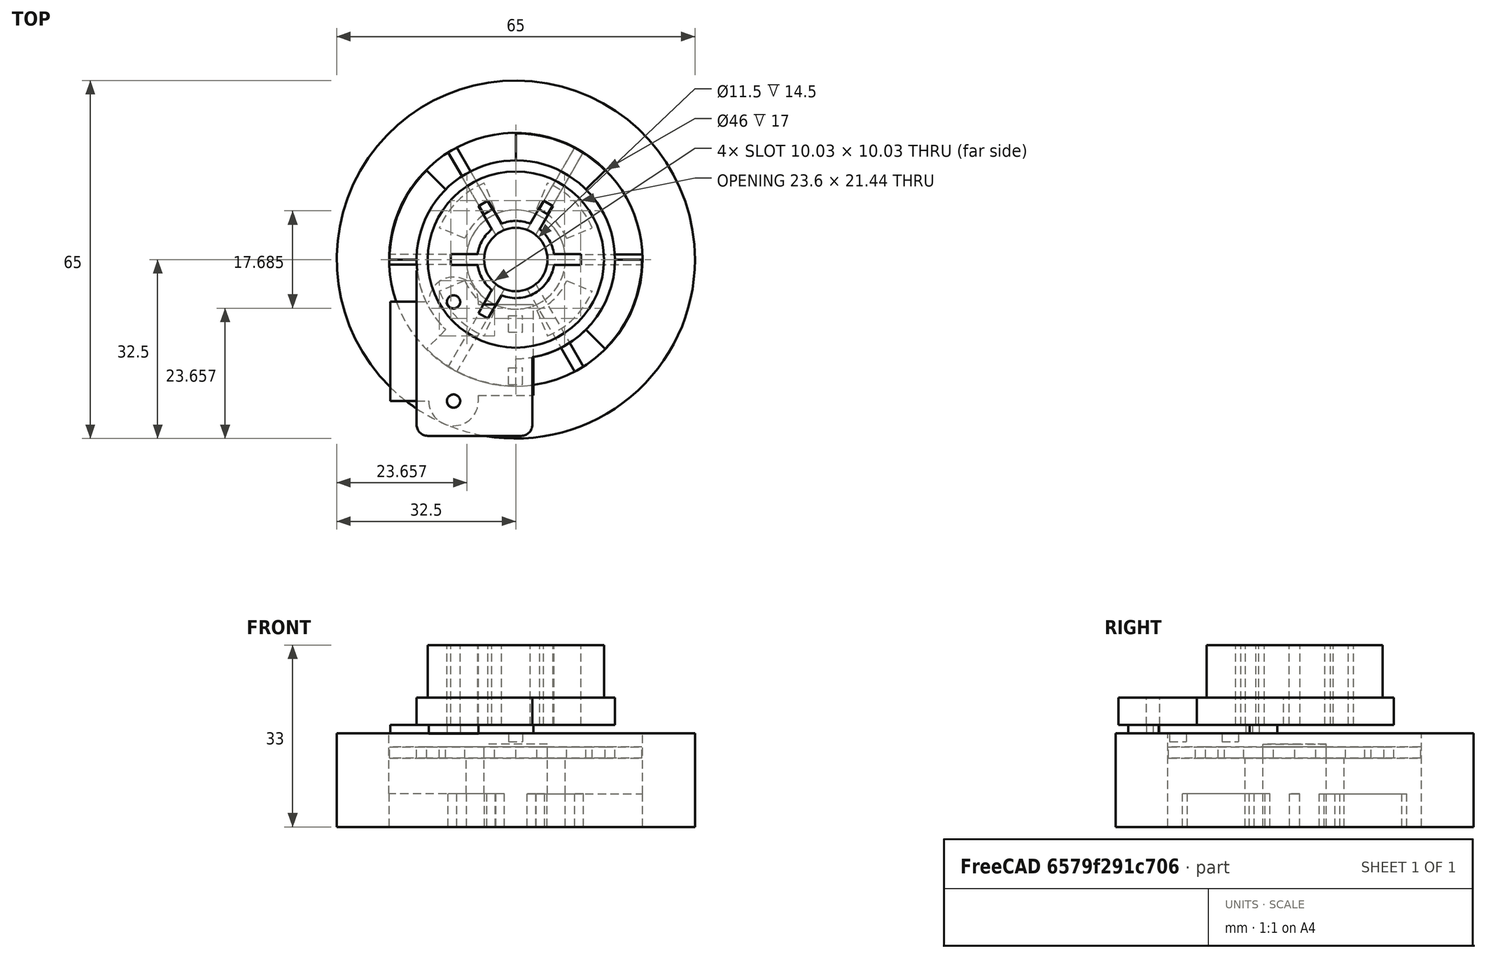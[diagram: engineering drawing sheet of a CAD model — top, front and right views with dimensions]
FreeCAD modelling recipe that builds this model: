
FCSTD DOCUMENT  (FreeCAD 0.15R4671 (Git))
Label: Encoder_wheel
License: All rights reserved
LicenseURL: http://es.wikipedia.org/wiki/Todos_los_derechos_reservados
objects: Part::Cylinder×14, Part::MultiFuse×10, Part::Cut×9, Part::Box×7, Part::FeaturePython×4, Part::Feature×2, Part::Extrusion×2, App::DocumentObjectGroup×1, Part::Fillet×1
note: 49 computed .brp shape members not serialized (recipe doc carries the construction recipe); baked Part::Feature solids carry a one-line shape summary decoded from their .brp

FEATURE [Part::Cylinder] Cylinder  label="Cilindro"
  Angle = 360
  Height = 15
  Radius = 5.75
FEATURE [Part::Box] Box  label="Cubo"
  Height = 6
  Length = 19
  Placement = pos=(5,-0.9,0) rot=(0,0,1;0rad)
  Width = 1.8
FEATURE [Part::FeaturePython] Array004  # Draft array (typed FeaturePython)
  Angle = 360
  ArrayType = 1
  Axis = (0,0,1)
  Base = -> Box
  Center = (0,0,0)
  Fuse = false
  IntervalAxis = (0,0,0)
  IntervalX = (1,0,0)
  IntervalY = (0,1,0)
  IntervalZ = (0,0,0)
  NumberPolar = 6
  NumberX = 2
  NumberY = 2
  NumberZ = 1
FEATURE [Part::MultiFuse] Fusion  label="Wheel_model"
  Shapes = -> [Cylinder,Array004]
FEATURE [Part::Cylinder] Cylinder002  label="Cilindro002"
  Angle = 360
  Height = 17
  Radius = 32.5
FEATURE [Part::Cylinder] Cylinder003  label="Cilindro003"
  Angle = 360
  Height = 17
  Radius = 23
FEATURE [Part::Cut] Cut003
  Base = -> Cylinder002
  Tool = -> Cylinder003
FEATURE [Part::MultiFuse] Fusion002  label="Wheel_model001"
  Shapes = -> [Cut003,Fusion]
FEATURE [Part::Cylinder] Cylinder004  label="Cilindro004"
  Angle = 360
  Height = 20
  Radius = 7
FEATURE [Part::Box] Box001  label="Cubo001"
  Height = 20
  Length = 5
  Placement = pos=(6.8,-1,0) rot=(0,0,1;0rad)
  Width = 2
FEATURE [Part::FeaturePython] Array006  # Draft array (typed FeaturePython)
  Angle = 240
  ArrayType = 1
  Axis = (0,0,1)
  Base = -> Box001
  Center = (0,0,0)
  Fuse = false
  IntervalAxis = (0,0,0)
  IntervalX = (1,0,0)
  IntervalY = (0,1,0)
  IntervalZ = (0,0,0)
  NumberPolar = 5
  NumberX = 2
  NumberY = 2
  NumberZ = 1
FEATURE [Part::Cylinder] Cylinder005  label="Cilindro005"
  Angle = 360
  Height = 5
  Placement = pos=(0,0,13.5) rot=(0,0,1;0rad)
  Radius = 18
FEATURE [Part::Cylinder] Cylinder006  label="Cilindro006"
  Angle = 360
  Height = 10
  Placement = pos=(0,0,18) rot=(0,0,1;0rad)
  Radius = 16
FEATURE [Part::MultiFuse] Fusion009  label="Axle_Model"
  Placement = pos=(0,0,13) rot=(0,0,1;0rad)
  Shapes = -> [Array006,Cylinder004]
FEATURE [Part::Feature] Face002
  shape: bbox 13.41 x 13.41 x 2e-07 mm, 1 faces, 0 solids (baked)
FEATURE [Part::Feature] Face003
  shape: bbox 20.57 x 13.88 x 2e-07 mm, 1 faces, 0 solids (baked)
FEATURE [Part::Extrusion] Extrude
  Base = -> Face002
  Dir = (0,0,2)
  Solid = true
FEATURE [Part::Extrusion] Extrude007
  Base = -> Face003
  Dir = (0,0,2)
  Solid = true
FEATURE [Part::Cylinder] Cylinder007  label="Cilindro007"
  Angle = 360
  Height = 2
  Radius = 22.9
FEATURE [Part::FeaturePython] Array007  # Draft array (typed FeaturePython)
  Angle = 360
  ArrayType = 1
  Axis = (0,0,1)
  Base = -> Extrude007
  Center = (0,0,0)
  Fuse = false
  IntervalAxis = (0,0,0)
  IntervalX = (1,0,0)
  IntervalY = (0,1,0)
  IntervalZ = (0,0,0)
  NumberPolar = 4
  NumberX = 2
  NumberY = 2
  NumberZ = 1
FEATURE [Part::FeaturePython] Array008  # Draft array (typed FeaturePython)
  Angle = 360
  ArrayType = 1
  Axis = (0,0,1)
  Base = -> Extrude
  Center = (0,0,0)
  Fuse = false
  IntervalAxis = (0,0,0)
  IntervalX = (1,0,0)
  IntervalY = (0,1,0)
  IntervalZ = (0,0,0)
  NumberPolar = 4
  NumberX = 2
  NumberY = 2
  NumberZ = 1
FEATURE [Part::Cut] Cut010
  Base = -> Cylinder007
  Tool = -> Array007
FEATURE [Part::Cut] Cut011  label="EncoderDisc"
  Base = -> Cut010
  Placement = pos=(0,0,12.5) rot=(0,0,1;0rad)
  Tool = -> Array008
FEATURE [Part::Cylinder] Cylinder008  label="DiscAxle"
  Angle = 360
  Height = 14.5
  Radius = 9
FEATURE [Part::MultiFuse] Fusion010
  Shapes = -> [Cut011,Cylinder008]
FEATURE [Part::Cut] Cut012  label="EncoderModel"
  Base = -> Fusion010
  Tool = -> Fusion
FEATURE [Part::Box] Box013  label="Cubo013"
  Height = 1.54
  Length = 18
  Width = 16
FEATURE [Part::Cylinder] Cylinder009  label="Cilindro008"
  Angle = 360
  Height = 1.54
  Placement = pos=(0,11.5,0) rot=(0,0,1;0rad)
  Radius = 1.2
FEATURE [Part::Cylinder] Cylinder010  label="Cilindro009"
  Angle = 360
  Height = 1.54
  Placement = pos=(18,11.5,0) rot=(0,0,1;0rad)
  Radius = 1.2
FEATURE [Part::Cylinder] Cylinder011  label="Cilindro010"
  Angle = 360
  Height = 1.54
  Placement = pos=(0,11.5,0) rot=(0,0,1;0rad)
  Radius = 4.5
FEATURE [Part::Cylinder] Cylinder012  label="Cilindro011"
  Angle = 360
  Height = 1.54
  Placement = pos=(18,11.5,0) rot=(0,0,1;0rad)
  Radius = 4.5
FEATURE [Part::Box] Box014  label="Cubo014"
  Height = 1.5
  Length = 3
  Placement = pos=(3,21.5,1.54) rot=(0,0,1;0rad)
  Width = 2.5
FEATURE [Part::Box] Box015  label="Cubo015"
  Height = 1.5
  Length = 3
  Placement = pos=(12.5,21.5,1.54) rot=(0,0,1;0rad)
  Width = 2.5
FEATURE [Part::Box] Box016  label="Cubo016"
  Height = 1.54
  Length = 16.5
  Placement = pos=(1,16,0) rot=(0,0,1;0rad)
  Width = 10
FEATURE [Part::MultiFuse] Fusion011
  Shapes = -> [Box016,Box013]
FEATURE [Part::MultiFuse] Fusion012
  Shapes = -> [Fusion011,Cylinder012]
FEATURE [Part::MultiFuse] Fusion013
  Shapes = -> [Fusion012,Cylinder011]
FEATURE [Part::Cut] Cut013
  Base = -> Fusion013
  Tool = -> Cylinder010
FEATURE [Part::Cut] Cut014
  Base = -> Cut013
  Tool = -> Cylinder009
FEATURE [Part::MultiFuse] Fusion014  label="SensorModel"
  Placement = pos=(-22.7908,-25.6736,18.5) rot=(0.707106,0.707107,0;3.14159rad)
  Shapes = -> [Cut014,Box015,Box014]
FEATURE [App::DocumentObjectGroup] Grupo  label="Model"
  Group = -> [Fusion014,Fusion002]
FEATURE [Part::Box] Box017  label="Cubo017"
  Height = 5
  Length = 21
  Placement = pos=(-18,-32,13.5) rot=(0,0,1;0rad)
  Width = 30
FEATURE [Part::MultiFuse] Fusion015
  Shapes = -> [Cylinder005,Cylinder006]
FEATURE [Part::MultiFuse] Fusion016
  Placement = pos=(0,0,5) rot=(0,0,1;0rad)
  Shapes = -> [Box017,Fusion015]
FEATURE [Part::Cylinder] Cylinder013  label="Cilindro012"
  Angle = 360
  Height = 20
  Placement = pos=(-11.3,-7.7,14) rot=(0,0,1;0rad)
  Radius = 1.2
FEATURE [Part::Cylinder] Cylinder014  label="Cilindro013"
  Angle = 360
  Height = 10
  Placement = pos=(-11.3,-25.7,14) rot=(0,0,1;0rad)
  Radius = 1.2
FEATURE [Part::Cut] Cut015
  Base = -> Fusion016
  Tool = -> Cylinder013
FEATURE [Part::Cut] Cut016
  Base = -> Cut015
  Tool = -> Cylinder014
FEATURE [Part::Cut] Cut
  Base = -> Cut016
  Tool = -> Fusion009
FEATURE [Part::Fillet] Fillet  label="SensorSupport"
  Base = -> Cut
  Edges = 2 edges r=2: [Edge1,Edge6]
